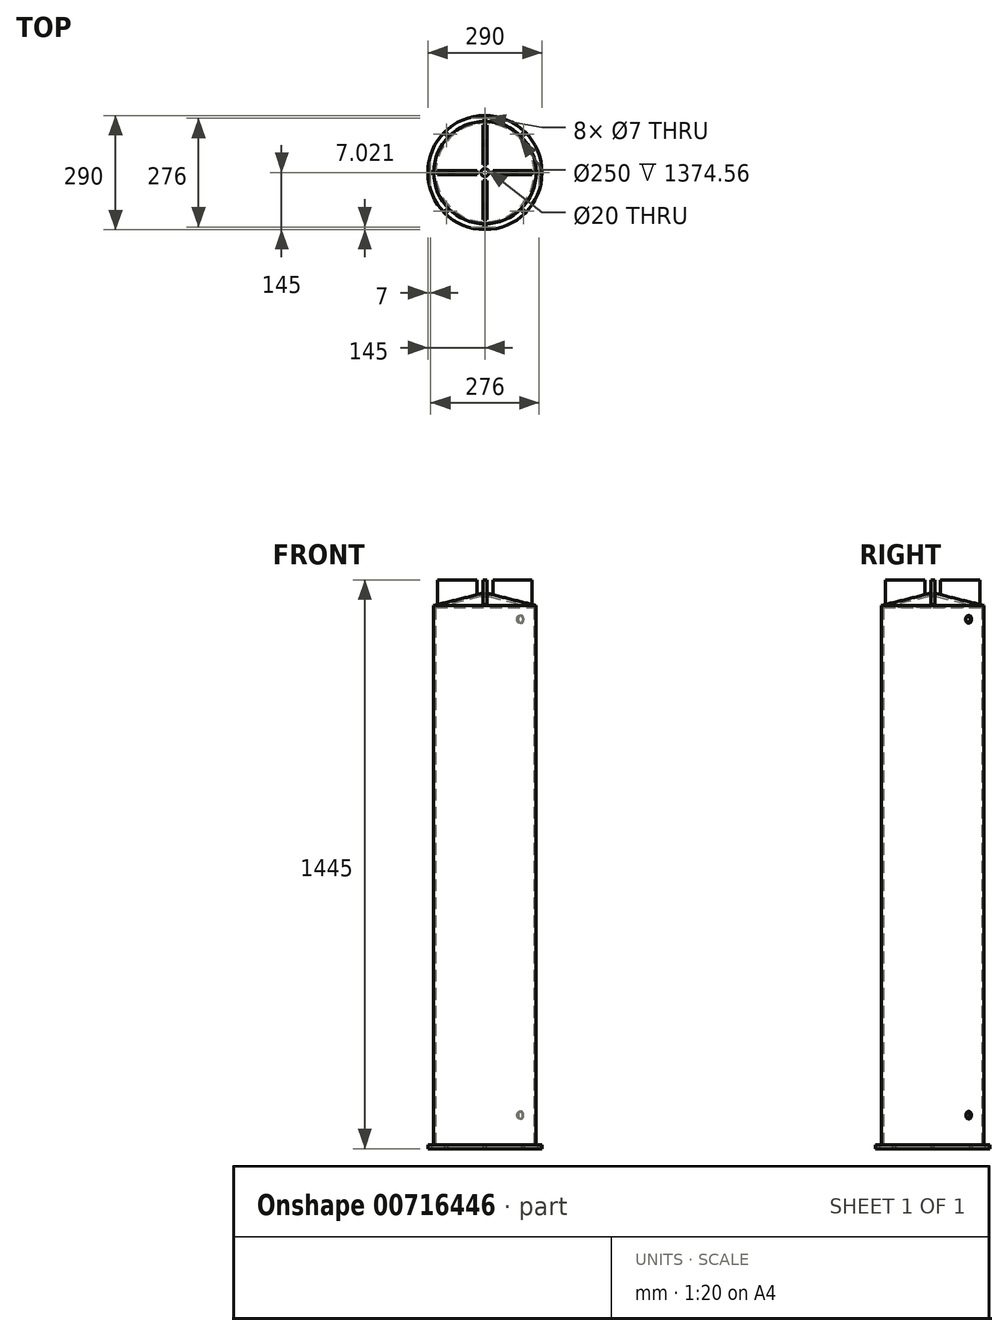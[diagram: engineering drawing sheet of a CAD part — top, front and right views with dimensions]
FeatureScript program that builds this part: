
annotation { "Feature Type Name" : "Feature", "Feature Type Description" : "" }
export const myFeature = defineFeature(function(context is Context, id is Id, definition is map)
    precondition{}
    {
        {
            var Q0;
            Q0=qCreatedBy(makeId("Top.planeOp"),FACE);
            var sketch = newSketch(context, id + "F0", { "sketchPlane" : qUnion([Q0])});
            skCircle(sketch, "E0", {"center": v(0, 0) * mm, "radius": 130 * mm});
            skSolve(sketch);
        }
        {
            var Q0;
            Q0 = qSketchRegion(id + "F0", true);
            extrude(context, id + "F1", {"entities" : qUnion([Q0]), "depth" : 1400 * mm, "offsetDistance" : 25 * mm});
        }
        {
            var Q0;
            Q0=makeQuery(id+"F1.opExtrude","CAP_EDGE",EDGE,{"disambiguationData":[OSD([sQuery(id+"F0.wireOp",EDGE,"E0")])],"isStart":false});
            chamfer(context, id + "F2", {"entities" : qUnion([Q0]), "chamferType" : ChamferType.TWO_OFFSETS, "width1" : 120 * mm, "oppositeDirection" : false, "width2" : 30 * mm, "tangentPropagation" : true});
        }
        {
            var Q0;
            Q0=makeQuery(id+"F1.opExtrude","CAP_FACE",FACE,{"disambiguationData":[OSD([sQuery(id+"F0.wireOp",EDGE,"E0")])],"isStart":false});
            var sketch = newSketch(context, id + "F3", { "sketchPlane" : qUnion([Q0])});
            skLineSegment(sketch, "E1", {"start": v(0, 0) * mm, "end": v(119.55, 0) * mm, "construction": true});
            skLineSegment(sketch, "E2.bottom", {"start": v(20, -5) * mm, "end": v(120, -5) * mm});
            skLineSegment(sketch, "E2.top", {"start": v(20, 5) * mm, "end": v(120, 5) * mm});
            skLineSegment(sketch, "E2.left", {"start": v(20, -5) * mm, "end": v(20, 5) * mm});
            skLineSegment(sketch, "E2.right", {"start": v(120, -5) * mm, "end": v(120, 5) * mm});
            skPoint(sketch, "E2.middle", {"position": v(70, 0) * mm});
            skPoint(sketch, "E3.1.0", {"position": v(0, 70) * mm});
            skLineSegment(sketch, "E3.1.1", {"start": v(5, 20) * mm, "end": v(-5, 20) * mm});
            skLineSegment(sketch, "E3.1.2", {"start": v(0, 0) * mm, "end": v(0, 119.55) * mm, "construction": true});
            skLineSegment(sketch, "E3.1.3", {"start": v(-5, 20) * mm, "end": v(-5, 120) * mm});
            skLineSegment(sketch, "E3.1.4", {"start": v(5, 20) * mm, "end": v(5, 120) * mm});
            skLineSegment(sketch, "E3.1.5", {"start": v(5, 120) * mm, "end": v(-5, 120) * mm});
            skPoint(sketch, "E3.2.0", {"position": v(-70, 0) * mm});
            skLineSegment(sketch, "E3.2.1", {"start": v(-20, 5) * mm, "end": v(-20, -5) * mm});
            skLineSegment(sketch, "E3.2.2", {"start": v(0, 0) * mm, "end": v(-119.55, 0) * mm, "construction": true});
            skLineSegment(sketch, "E3.2.3", {"start": v(-20, -5) * mm, "end": v(-120, -5) * mm});
            skLineSegment(sketch, "E3.2.4", {"start": v(-20, 5) * mm, "end": v(-120, 5) * mm});
            skLineSegment(sketch, "E3.2.5", {"start": v(-120, 5) * mm, "end": v(-120, -5) * mm});
            skPoint(sketch, "E3.3.0", {"position": v(0, -70) * mm});
            skLineSegment(sketch, "E3.3.1", {"start": v(-5, -20) * mm, "end": v(5, -20) * mm});
            skLineSegment(sketch, "E3.3.2", {"start": v(0, 0) * mm, "end": v(0, -119.55) * mm, "construction": true});
            skLineSegment(sketch, "E3.3.3", {"start": v(5, -20) * mm, "end": v(5, -120) * mm});
            skLineSegment(sketch, "E3.3.4", {"start": v(-5, -20) * mm, "end": v(-5, -120) * mm});
            skLineSegment(sketch, "E3.3.5", {"start": v(-5, -120) * mm, "end": v(5, -120) * mm});
            skPoint(sketch, "E3.center", {"position": v(0, 0) * mm});
            skSolve(sketch);
        }
        {
            var Q0;
            Q0 = qSketchRegion(id + "F3", true);
            extrude(context, id + "F4", {"entities" : qUnion([Q0]), "operationType" : NewBodyOperationType.ADD, "depth" : 35 * mm, "offsetDistance" : 25 * mm, "hasSecondDirection" : true, "secondDirectionOppositeDirection" : true, "secondDirectionDepth" : 35 * mm});
        }
        {
            var Q0;
            Q0=qCreatedBy(makeId("Right.planeOp"),FACE);
            var sketch = newSketch(context, id + "F5", { "sketchPlane" : qUnion([Q0])});
            skLineSegment(sketch, "E4", {"start": v(0, 0) * mm, "end": v(-125, 0) * mm});
            skLineSegment(sketch, "E5", {"start": v(-125, 0) * mm, "end": v(-125, 1364.56) * mm});
            skLineSegment(sketch, "E6", {"start": v(-125, 1364.56) * mm, "end": v(0, 1395) * mm});
            skLineSegment(sketch, "E7", {"start": v(0, 0) * mm, "end": v(0, 1395) * mm});
            skSolve(sketch);
        }
        {
            var Q0;
            Q0=qCreatedBy(makeId("Right.planeOp"),FACE);
            var sketch = newSketch(context, id + "F6", { "sketchPlane" : qUnion([Q0])});
            skLineSegment(sketch, "E8", {"start": v(0, 1419.92) * mm, "end": v(0, -58.47) * mm, "construction": true});
            skSolve(sketch);
        }
        {
            var Q0;
            Q0 = qSketchRegion(id + "F5", true);
            var Q1;
            Q1=sQuery(id+"F6.wireOp",EDGE,"E8");
            revolve(context, id + "F7", {"operationType" : NewBodyOperationType.REMOVE, "surfaceOperationType" : NewSurfaceOperationType.NEW, "entities" : qUnion([Q0]), "axis" : qUnion([Q1]), "revolveType" : RevolveType.FULL, "oppositeDirection" : true});
        }
        {
            var Q0;
            Q0=makeQuery(id+"F1.opExtrude","CAP_FACE",FACE,{"disambiguationData":[OSD([sQuery(id+"F0.wireOp",EDGE,"E0")])],"isStart":true});
            var sketch = newSketch(context, id + "F8", { "sketchPlane" : qUnion([Q0])});
            skCircle(sketch, "E9", {"center": v(0, 0) * mm, "radius": 145 * mm});
            skCircle(sketch, "E10", {"center": v(0, 0) * mm, "radius": 125 * mm});
            skCircle(sketch, "E11", {"center": v(0, -138.02) * mm, "radius": 3.5 * mm});
            skCircle(sketch, "E12.1.0", {"center": v(97.58, -97.6) * mm, "radius": 3.5 * mm});
            skCircle(sketch, "E12.2.0", {"center": v(138, -0.02) * mm, "radius": 3.5 * mm});
            skCircle(sketch, "E12.3.0", {"center": v(97.58, 97.56) * mm, "radius": 3.5 * mm});
            skCircle(sketch, "E12.4.0", {"center": v(0, 137.98) * mm, "radius": 3.5 * mm});
            skCircle(sketch, "E12.5.0", {"center": v(-97.58, 97.56) * mm, "radius": 3.5 * mm});
            skCircle(sketch, "E12.6.0", {"center": v(-138, -0.02) * mm, "radius": 3.5 * mm});
            skCircle(sketch, "E12.7.0", {"center": v(-97.58, -97.6) * mm, "radius": 3.5 * mm});
            skPoint(sketch, "E12.center", {"position": v(0, -0.02) * mm});
            skSolve(sketch);
        }
        {
            var Q0;
            Q0 = qSketchRegion(id + "F8", true);
            extrude(context, id + "F9", {"entities" : qUnion([Q0]), "operationType" : NewBodyOperationType.ADD, "depth" : 10 * mm, "offsetDistance" : 25 * mm});
        }
        {
            var Q0;
            Q0=makeQuery(id+"F1.opExtrude","CAP_FACE",FACE,{"disambiguationData":[OSD([sQuery(id+"F0.wireOp",EDGE,"E0")])],"isStart":false});
            var sketch = newSketch(context, id + "F10", { "sketchPlane" : qUnion([Q0])});
            skCircle(sketch, "E13", {"center": v(0, 0) * mm, "radius": 10 * mm});
            skSolve(sketch);
        }
        {
            var Q0;
            Q0=qCreatedBy(makeId("Right.planeOp"),FACE);
            var sketch = newSketch(context, id + "F11", { "sketchPlane" : qUnion([Q0])});
            skLineSegment(sketch, "E14", {"start": v(0, -77.38) * mm, "end": v(0, 1493.3) * mm, "construction": true});
            skSolve(sketch);
        }
        {
            var Q0;
            Q0 = qSketchRegion(id + "F10", true);
            extrude(context, id + "F12", {"entities" : qUnion([Q0]), "operationType" : NewBodyOperationType.REMOVE, "oppositeDirection" : true, "depth" : 25 * mm, "offsetDistance" : 25 * mm});
        }
        {
            var Q0;
            Q0=qCreatedBy(makeId("Right.planeOp"),FACE);
            var Q1;
            Q1=sQuery(id+"F11.wireOp",EDGE,"E14");
            cPlane(context, id + "F13", {"entities" : qUnion([Q0, Q1]), "cplaneType" : CPlaneType.LINE_ANGLE, "offset" : 25 * mm, "angle" : 45 * degree, "width" : 150 * mm, "height" : 150 * mm});
        }
        {
            var Q0;
            Q0=qCreatedBy(id+"F13.planeOp",FACE);
            var sketch = newSketch(context, id + "F14", { "sketchPlane" : qUnion([Q0])});
            skCircle(sketch, "E15", {"center": v(0, 75) * mm, "radius": 9.5 * mm});
            skCircle(sketch, "E16", {"center": v(0, 1335) * mm, "radius": 10 * mm});
            skSolve(sketch);
        }
        {
            var Q0;
            Q0 = qSketchRegion(id + "F14", true);
            extrude(context, id + "F15", {"entities" : qUnion([Q0]), "operationType" : NewBodyOperationType.REMOVE, "oppositeDirection" : true, "depth" : 225 * mm, "offsetDistance" : 25 * mm});
        }
    });
